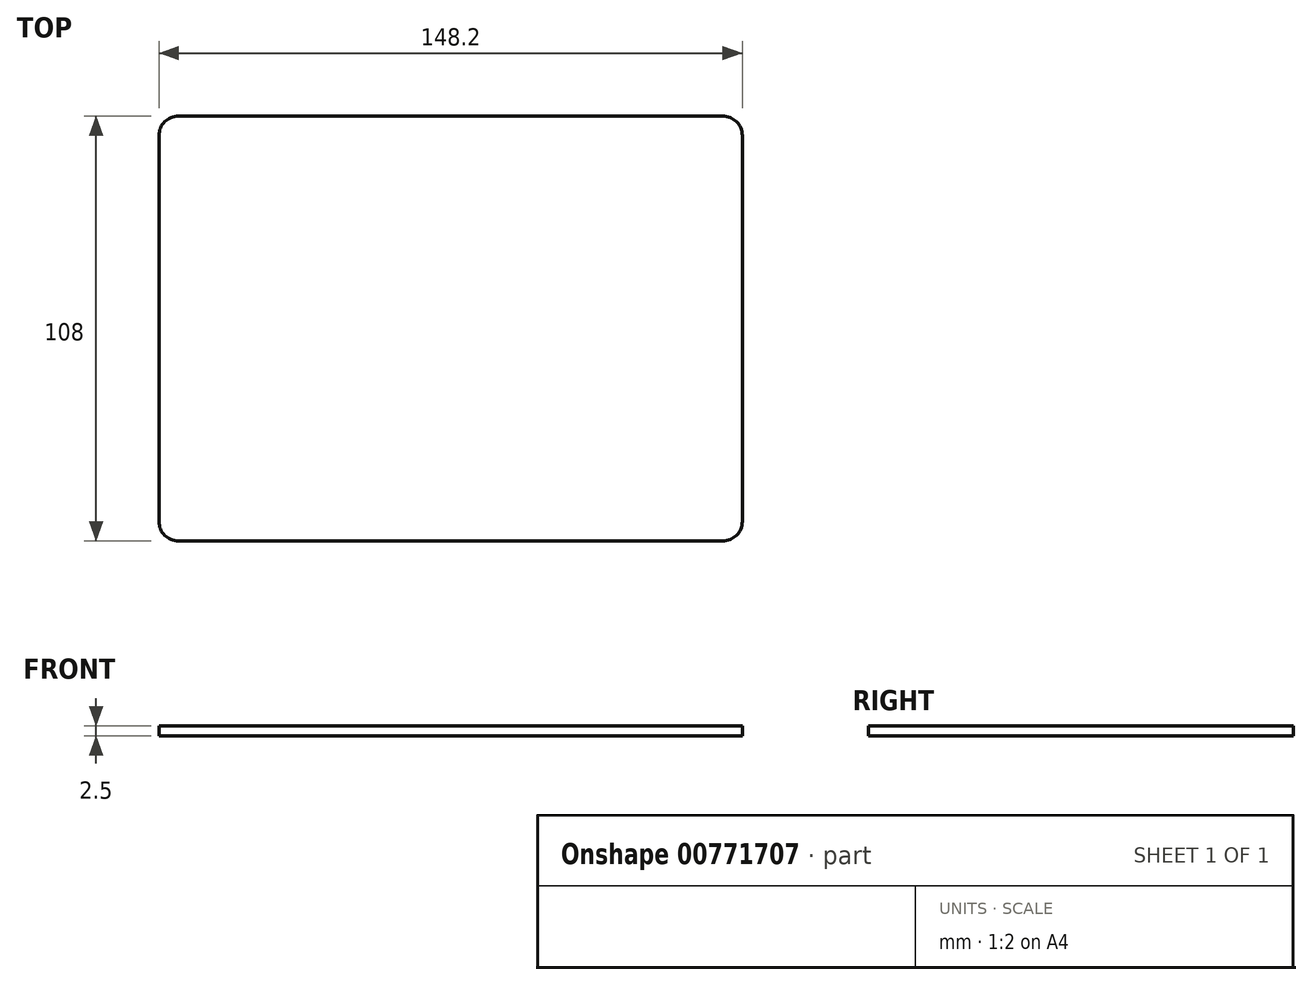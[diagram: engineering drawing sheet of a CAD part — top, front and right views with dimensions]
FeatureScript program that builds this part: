
annotation { "Feature Type Name" : "Feature", "Feature Type Description" : "" }
export const myFeature = defineFeature(function(context is Context, id is Id, definition is map)
    precondition{}
    {
        {
            var Q0;
            Q0=qCreatedBy(makeId("Top.planeOp"),FACE);
            var sketch = newSketch(context, id + "F0", { "sketchPlane" : qUnion([Q0])});
            skLineSegment(sketch, "E0.bottom", {"start": v(-69.1, 54) * mm, "end": v(69.1, 54) * mm});
            skLineSegment(sketch, "E0.top", {"start": v(-69.1, -54) * mm, "end": v(69.1, -54) * mm});
            skLineSegment(sketch, "E0.left", {"start": v(-74.1, 49) * mm, "end": v(-74.1, -49) * mm});
            skLineSegment(sketch, "E0.right", {"start": v(74.1, 49) * mm, "end": v(74.1, -49) * mm});
            skPoint(sketch, "E0.middle", {"position": v(0, 0) * mm});
            skPoint(sketch, "E1.visualSharp", {"position": v(-74.1, 54) * mm});
            skArc(sketch, "E1.filletArc", {"start": v(-69.1, 54) * mm, "mid": v(-72.64, 52.54) * mm, "end": v(-74.1, 49) * mm});
            skPoint(sketch, "E2.visualSharp", {"position": v(-74.1, -54) * mm});
            skArc(sketch, "E2.filletArc", {"start": v(-74.1, -49) * mm, "mid": v(-72.64, -52.54) * mm, "end": v(-69.1, -54) * mm});
            skPoint(sketch, "E3.visualSharp", {"position": v(74.1, -54) * mm});
            skArc(sketch, "E3.filletArc", {"start": v(69.1, -54) * mm, "mid": v(72.64, -52.54) * mm, "end": v(74.1, -49) * mm});
            skPoint(sketch, "E4.visualSharp", {"position": v(74.1, 54) * mm});
            skArc(sketch, "E4.filletArc", {"start": v(74.1, 49) * mm, "mid": v(72.64, 52.54) * mm, "end": v(69.1, 54) * mm});
            skSolve(sketch);
        }
        {
            var Q0;
            Q0=makeQuery(id+"F0.imprint","IMPRINT",FACE,{"disambiguationData":[TD([[makeQuery(id+"F0.imprint","IMPRINT",EDGE,{"derivedFrom":sQuery(id+"F0.wireOp",EDGE,"E0.bottom")}),-1.0]])]});
            extrude(context, id + "F1", {"entities" : qUnion([Q0]), "depth" : 2.5 * mm, "offsetDistance" : 25 * mm});
        }
    });
